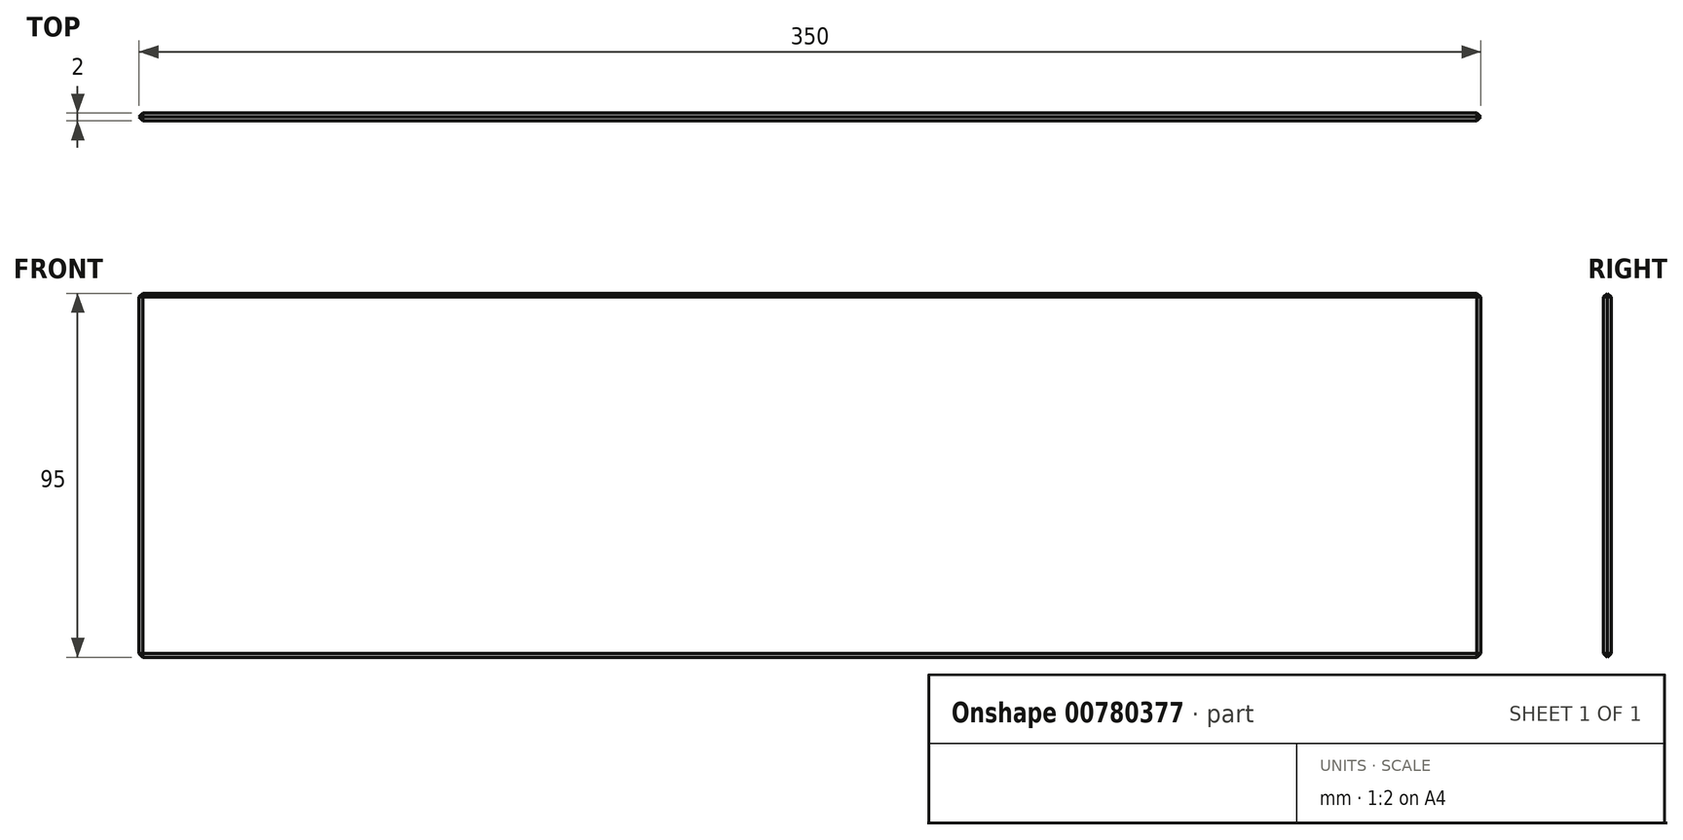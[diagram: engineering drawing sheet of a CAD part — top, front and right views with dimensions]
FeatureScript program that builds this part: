
annotation { "Feature Type Name" : "Feature", "Feature Type Description" : "" }
export const myFeature = defineFeature(function(context is Context, id is Id, definition is map)
    precondition{}
    {
        {
            var Q0;
            Q0=qCreatedBy(makeId("Front.planeOp"),FACE);
            var sketch = newSketch(context, id + "F0", { "sketchPlane" : qUnion([Q0])});
            skLineSegment(sketch, "E0.bottom", {"start": v(-175, 47.5) * mm, "end": v(175, 47.5) * mm});
            skLineSegment(sketch, "E0.top", {"start": v(-175, -47.5) * mm, "end": v(175, -47.5) * mm});
            skLineSegment(sketch, "E0.left", {"start": v(-175, 47.5) * mm, "end": v(-175, -47.5) * mm});
            skLineSegment(sketch, "E0.right", {"start": v(175, 47.5) * mm, "end": v(175, -47.5) * mm});
            skPoint(sketch, "E0.middle", {"position": v(0, 0) * mm});
            skSolve(sketch);
        }
        {
            var Q0;
            Q0=makeQuery(id+"F0.imprint","IMPRINT",FACE,{"disambiguationData":[TD([[makeQuery(id+"F0.imprint","IMPRINT",EDGE,{"derivedFrom":sQuery(id+"F0.wireOp",EDGE,"E0.bottom")}),-1.0]])]});
            extrude(context, id + "F1", {"entities" : qUnion([Q0]), "depth" : 2 * mm, "offsetDistance" : 25 * mm});
        }
        {
            var Q0;
            Q0=makeQuery(id+"F1.opExtrude","CAP_EDGE",EDGE,{"disambiguationData":[OSD([sQuery(id+"F0.wireOp",EDGE,"E0.left")])],"isStart":false});
            var Q1;
            Q1=makeQuery(id+"F1.opExtrude","CAP_FACE",FACE,{"disambiguationData":[OSD([sQuery(id+"F0.wireOp",EDGE,"E0.bottom"),sQuery(id+"F0.wireOp",EDGE,"E0.top"),sQuery(id+"F0.wireOp",EDGE,"E0.left"),sQuery(id+"F0.wireOp",EDGE,"E0.right")])],"isStart":false});
            var Q2;
            Q2=makeQuery(id+"F1.opExtrude","CAP_EDGE",EDGE,{"disambiguationData":[OSD([sQuery(id+"F0.wireOp",EDGE,"E0.left")])],"isStart":true});
            var Q3;
            Q3=makeQuery(id+"F1.opExtrude","CAP_EDGE",EDGE,{"disambiguationData":[OSD([sQuery(id+"F0.wireOp",EDGE,"E0.bottom")])],"isStart":true});
            var Q4;
            Q4=makeQuery(id+"F1.opExtrude","CAP_EDGE",EDGE,{"disambiguationData":[OSD([sQuery(id+"F0.wireOp",EDGE,"E0.right")])],"isStart":true});
            var Q5;
            Q5=makeQuery(id+"F1.opExtrude","CAP_EDGE",EDGE,{"disambiguationData":[OSD([sQuery(id+"F0.wireOp",EDGE,"E0.top")])],"isStart":true});
            var Q6;
            Q6=makeQuery(id+"F1.opExtrude","SWEPT_EDGE",EDGE,{"disambiguationData":[OSD([sQuery(id+"F0.wireOp",EDGE,"E0.top"),sQuery(id+"F0.wireOp",EDGE,"E0.right")])]});
            var Q7;
            Q7=makeQuery(id+"F1.opExtrude","SWEPT_EDGE",EDGE,{"disambiguationData":[OSD([sQuery(id+"F0.wireOp",EDGE,"E0.bottom"),sQuery(id+"F0.wireOp",EDGE,"E0.right")])]});
            var Q8;
            Q8=makeQuery(id+"F1.opExtrude","SWEPT_EDGE",EDGE,{"disambiguationData":[OSD([sQuery(id+"F0.wireOp",EDGE,"E0.top"),sQuery(id+"F0.wireOp",EDGE,"E0.left")])]});
            var Q9;
            Q9=makeQuery(id+"F1.opExtrude","SWEPT_EDGE",EDGE,{"disambiguationData":[OSD([sQuery(id+"F0.wireOp",EDGE,"E0.bottom"),sQuery(id+"F0.wireOp",EDGE,"E0.left")])]});
            chamfer(context, id + "F2", {"entities" : qUnion([Q0, Q1, Q2, Q3, Q4, Q5, Q6, Q7, Q8, Q9]), "width" : 1 * mm, "tangentPropagation" : true});
        }
    });
